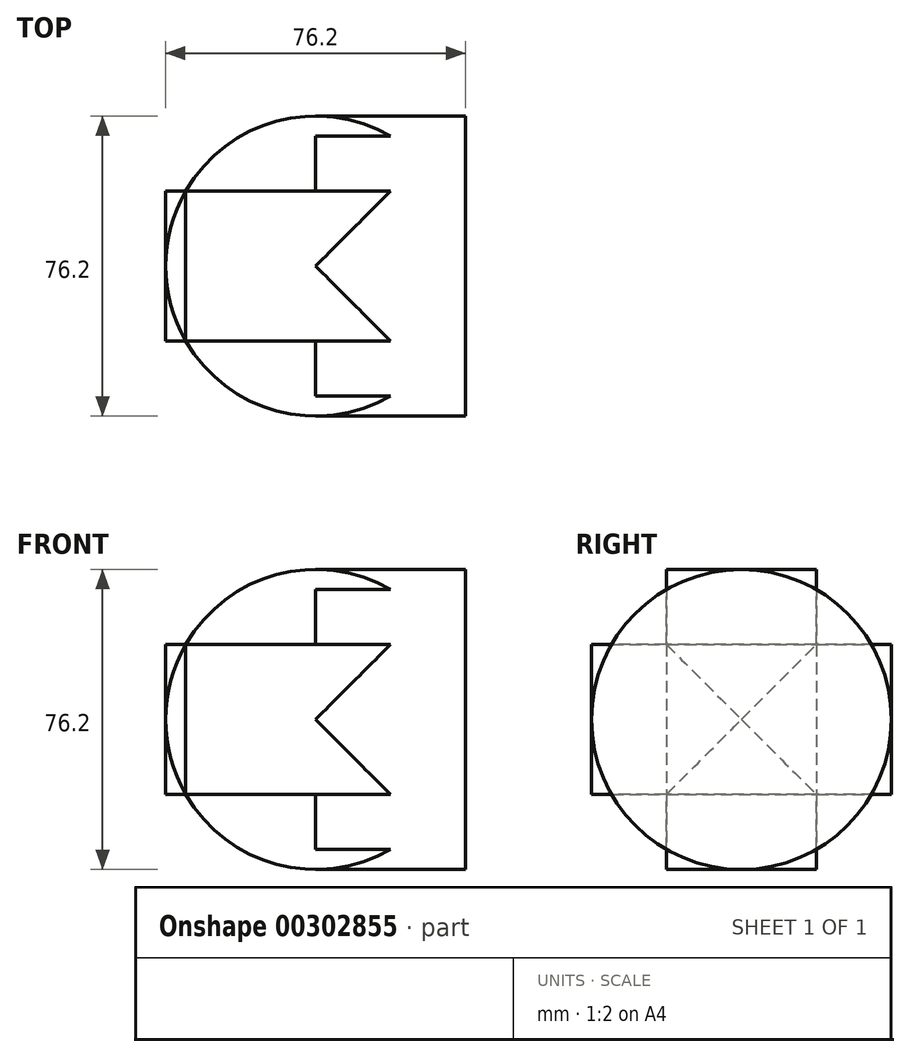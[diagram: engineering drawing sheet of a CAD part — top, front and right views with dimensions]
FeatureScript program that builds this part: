
annotation { "Feature Type Name" : "Feature", "Feature Type Description" : "" }
export const myFeature = defineFeature(function(context is Context, id is Id, definition is map)
    precondition{}
    {
        {
            var Q0;
            Q0=qCreatedBy(makeId("Front.planeOp"),FACE);
            var sketch = newSketch(context, id + "F0", { "sketchPlane" : qUnion([Q0])});
            skCircle(sketch, "E0", {"center": v(0, 0) * mm, "radius": 38.1 * mm});
            skSolve(sketch);
        }
        {
            var Q0;
            Q0=qCreatedBy(makeId("Top.planeOp"),FACE);
            var sketch = newSketch(context, id + "F1", { "sketchPlane" : qUnion([Q0])});
            skCircle(sketch, "E1", {"center": v(0, 0) * mm, "radius": 38.1 * mm});
            skSolve(sketch);
        }
        {
            var Q0;
            Q0=qCreatedBy(makeId("Right.planeOp"),FACE);
            var sketch = newSketch(context, id + "F2", { "sketchPlane" : qUnion([Q0])});
            skCircle(sketch, "E2", {"center": v(0, 0) * mm, "radius": 38.1 * mm});
            skSolve(sketch);
        }
        {
            var Q0;
            Q0=makeQuery(id+"F1.imprint","IMPRINT",FACE,{"disambiguationData":[TD([[makeQuery(id+"F1.imprint","IMPRINT",EDGE,{"derivedFrom":sQuery(id+"F1.wireOp",EDGE,"E1")}),1.0]])]});
            extrude(context, id + "F3", {"entities" : qUnion([Q0]), "endBound" : BoundingType.SYMMETRIC, "depth" : 38.1 * mm});
        }
        {
            var Q0;
            Q0 = qSketchRegion(id + "F0", true);
            extrude(context, id + "F4", {"entities" : qUnion([Q0]), "operationType" : NewBodyOperationType.ADD, "endBound" : BoundingType.SYMMETRIC, "depth" : 38.1 * mm});
        }
        {
            var Q0;
            Q0 = qSketchRegion(id + "F2", true);
            extrude(context, id + "F5", {"entities" : qUnion([Q0]), "operationType" : NewBodyOperationType.ADD, "depth" : 38.1 * mm});
        }
    });
